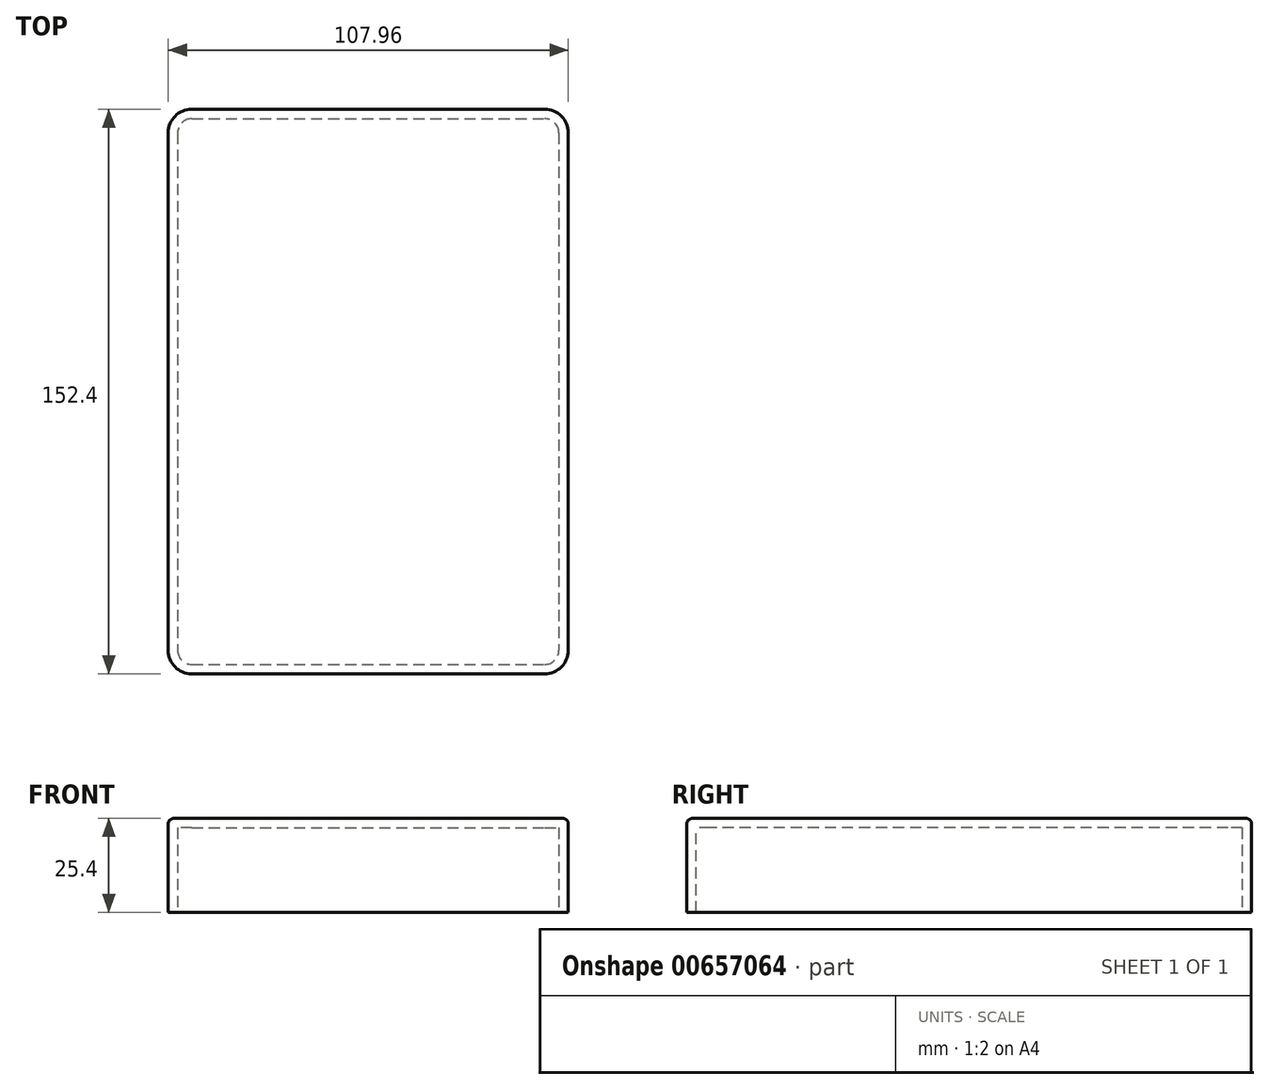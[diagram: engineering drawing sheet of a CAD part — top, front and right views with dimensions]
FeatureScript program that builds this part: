
annotation { "Feature Type Name" : "Feature", "Feature Type Description" : "" }
export const myFeature = defineFeature(function(context is Context, id is Id, definition is map)
    precondition{}
    {
        {
            var Q0;
            Q0=qCreatedBy(makeId("Top.planeOp"),FACE);
            var sketch = newSketch(context, id + "F0", { "sketchPlane" : qUnion([Q0])});
            skLineSegment(sketch, "E0.bottom", {"start": v(-47.62, 76.2) * mm, "end": v(47.62, 76.2) * mm});
            skLineSegment(sketch, "E0.top", {"start": v(-47.62, -76.2) * mm, "end": v(47.62, -76.2) * mm});
            skLineSegment(sketch, "E0.left", {"start": v(-53.97, 69.85) * mm, "end": v(-53.98, -69.85) * mm});
            skLineSegment(sketch, "E0.right", {"start": v(53.98, 69.85) * mm, "end": v(53.97, -69.85) * mm});
            skPoint(sketch, "E1.visualSharp", {"position": v(-53.97, 76.2) * mm});
            skArc(sketch, "E1.filletArc", {"start": v(-47.62, 76.2) * mm, "mid": v(-52.12, 74.34) * mm, "end": v(-53.98, 69.85) * mm});
            skPoint(sketch, "E2.visualSharp", {"position": v(53.98, 76.2) * mm});
            skArc(sketch, "E2.filletArc", {"start": v(53.97, 69.85) * mm, "mid": v(52.12, 74.34) * mm, "end": v(47.62, 76.2) * mm});
            skPoint(sketch, "E3.visualSharp", {"position": v(-53.98, -76.2) * mm});
            skArc(sketch, "E3.filletArc", {"start": v(-53.98, -69.85) * mm, "mid": v(-52.12, -74.34) * mm, "end": v(-47.62, -76.2) * mm});
            skPoint(sketch, "E4.visualSharp", {"position": v(53.98, -76.2) * mm});
            skArc(sketch, "E4.filletArc", {"start": v(47.62, -76.2) * mm, "mid": v(52.12, -74.34) * mm, "end": v(53.98, -69.85) * mm});
            skSolve(sketch);
        }
        {
            var Q0;
            Q0 = qSketchRegion(id + "F0", true);
            extrude(context, id + "F1", {"entities" : qUnion([Q0]), "depth" : 25.4 * mm, "offsetDistance" : 25.4 * mm});
        }
        {
            var Q0;
            Q0=makeQuery(id+"F1.opExtrude","CAP_EDGE",EDGE,{"disambiguationData":[OSD([sQuery(id+"F0.wireOp",EDGE,"E0.bottom")])],"isStart":false});
            fillet(context, id + "F2", {"entities" : qUnion([Q0]), "radius" : 1.52 * mm, "tangentPropagation" : true, "allowEdgeOverflow" : false});
        }
        {
            var Q0;
            Q0=makeQuery(id+"F1.opExtrude","CAP_FACE",FACE,{"disambiguationData":[OSD([sQuery(id+"F0.wireOp",EDGE,"E0.bottom"),sQuery(id+"F0.wireOp",EDGE,"E0.top"),sQuery(id+"F0.wireOp",EDGE,"E0.left"),sQuery(id+"F0.wireOp",EDGE,"E0.right"),sQuery(id+"F0.wireOp",EDGE,"E1.filletArc"),sQuery(id+"F0.wireOp",EDGE,"E2.filletArc"),sQuery(id+"F0.wireOp",EDGE,"E3.filletArc"),sQuery(id+"F0.wireOp",EDGE,"E4.filletArc")])],"isStart":true});
            shell(context, id + "F3", {"entities" : qUnion([Q0]), "thickness" : 2.54 * mm});
        }
    });
